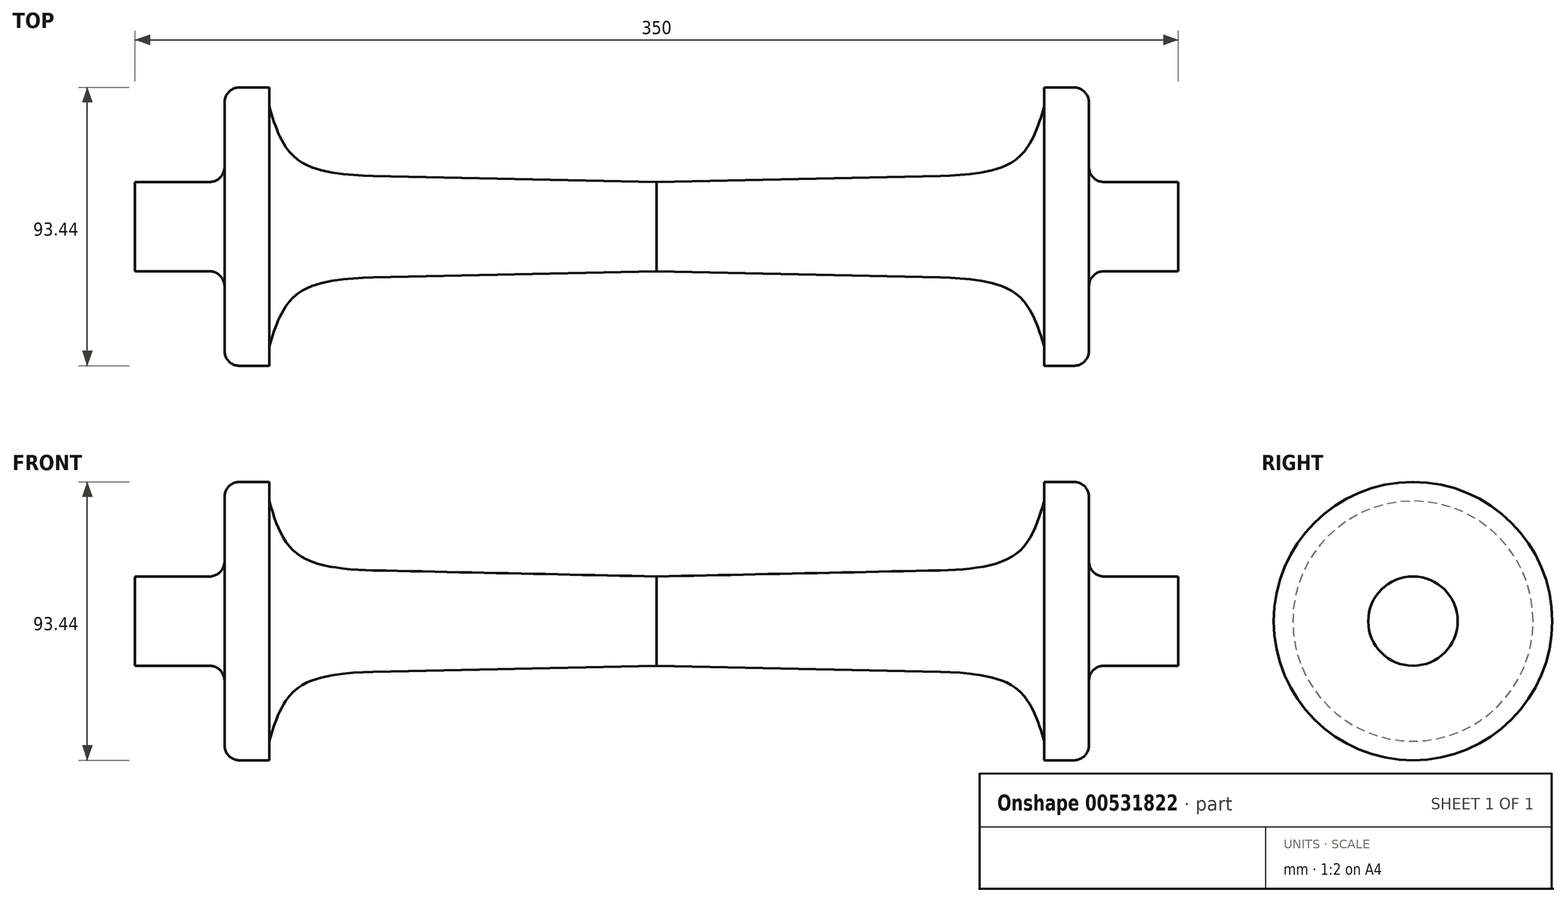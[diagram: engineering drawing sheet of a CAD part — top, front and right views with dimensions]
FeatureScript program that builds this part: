
annotation { "Feature Type Name" : "Feature", "Feature Type Description" : "" }
export const myFeature = defineFeature(function(context is Context, id is Id, definition is map)
    precondition{}
    {
        {
            var Q0;
            Q0=qCreatedBy(makeId("Front.planeOp"),FACE);
            var sketch = newSketch(context, id + "F0", { "sketchPlane" : qUnion([Q0])});
            skLineSegment(sketch, "E0", {"start": v(-113.25, 19.9) * mm, "end": v(-113.25, 4.9) * mm});
            skLineSegment(sketch, "E1", {"start": v(-113.25, 4.9) * mm, "end": v(61.75, 4.9) * mm});
            skLineSegment(sketch, "E2", {"start": v(61.75, 4.9) * mm, "end": v(61.75, 19.9) * mm});
            skLineSegment(sketch, "E3", {"start": v(26.75, 51.62) * mm, "end": v(16.75, 51.62) * mm});
            skLineSegment(sketch, "E4", {"start": v(16.75, 51.62) * mm, "end": v(16.75, 45.21) * mm});
            skLineSegment(sketch, "E5", {"start": v(-18.06, 21.92) * mm, "end": v(-113.25, 19.9) * mm});
            skFitSpline(sketch, "E6", {"points": [v(16.75, 45.21) * mm, v(6.96, 27.2) * mm, v(-25, 21.77) * mm], "startDerivative": vector(-14.3, -47.52) * mm, "endDerivative": vector(-67.18, -1.12) * mm});
            skPoint(sketch, "E7.visualSharp", {"position": v(77.37, 51.62) * mm});
            skLineSegment(sketch, "E8", {"start": v(31.75, 24.9) * mm, "end": v(31.75, 46.62) * mm});
            skPoint(sketch, "E9.visualSharp", {"position": v(31.75, 51.62) * mm});
            skArc(sketch, "E9.filletArc", {"start": v(31.75, 46.62) * mm, "mid": v(30.3, 50.15) * mm, "end": v(26.75, 51.62) * mm});
            skPoint(sketch, "E10.visualSharp", {"position": v(31.75, 19.9) * mm});
            skArc(sketch, "E10.filletArc", {"start": v(31.75, 24.9) * mm, "mid": v(33.22, 21.36) * mm, "end": v(36.75, 19.9) * mm});
            skLineSegment(sketch, "E11", {"start": v(36.75, 19.9) * mm, "end": v(61.75, 19.9) * mm});
            skSolve(sketch);
        }
        {
            var Q0;
            {var subQ5=sQuery(id+"F0.wireOp",EDGE,"E0");Q0=makeQuery(id+"F0.imprint","IMPRINT",FACE,{"disambiguationData":[TD([[makeQuery(id+"F0.imprint","IMPRINT",EDGE,{"derivedFrom":subQ5}),1.0]])]});}
            var Q1;
            {var subQ0=sQuery(id+"F0.wireOp",EDGE,"E6");var subQ1=sQuery(id+"F0.wireOp",EDGE,"E5");var subQ2=makeQuery(id+"F0.imprint","INTERSECT",VERTEX,{"disambiguationData":[OD(0.0)],"derivedFrom":[subQ1,subQ0]});Q1=makeQuery(id+"F0.imprint","IMPRINT",FACE,{"disambiguationData":[TD([[makeQuery(id+"F0.imprint","IMPRINT",EDGE,{"disambiguationData":[TD([[subQ2,-1.0]])],"derivedFrom":subQ1}),1.0]])]});}
            var Q2;
            Q2=sQuery(id+"F0.wireOp",EDGE,"E1");
            revolve(context, id + "F1", {"entities" : qUnion([Q0, Q1]), "axis" : qUnion([Q2]), "revolveType" : RevolveType.FULL});
        }
        {
            var Q0;
            Q0=makeQuery(id+"F1.opRevolve","SWEPT_BODY",BODY,{"disambiguationData":[OSD([sQuery(id+"F0.wireOp",EDGE,"E0"),sQuery(id+"F0.wireOp",EDGE,"E1"),sQuery(id+"F0.wireOp",EDGE,"E2"),sQuery(id+"F0.wireOp",EDGE,"E3"),sQuery(id+"F0.wireOp",EDGE,"E4"),sQuery(id+"F0.wireOp",EDGE,"E5"),sQuery(id+"F0.wireOp",EDGE,"E6"),sQuery(id+"F0.wireOp",EDGE,"E8"),sQuery(id+"F0.wireOp",EDGE,"E9.filletArc"),sQuery(id+"F0.wireOp",EDGE,"E10.filletArc"),sQuery(id+"F0.wireOp",EDGE,"E11")])]});
            var Q1;
            Q1=makeQuery(id+"F1.opRevolve","SWEPT_FACE",FACE,{"disambiguationData":[OSD([sQuery(id+"F0.wireOp",EDGE,"E0")])]});
            mirror(context, id + "F2", {"operationType" : NewBodyOperationType.ADD, "entities" : qUnion([Q0]), "mirrorPlane" : qUnion([Q1])});
        }
    });
